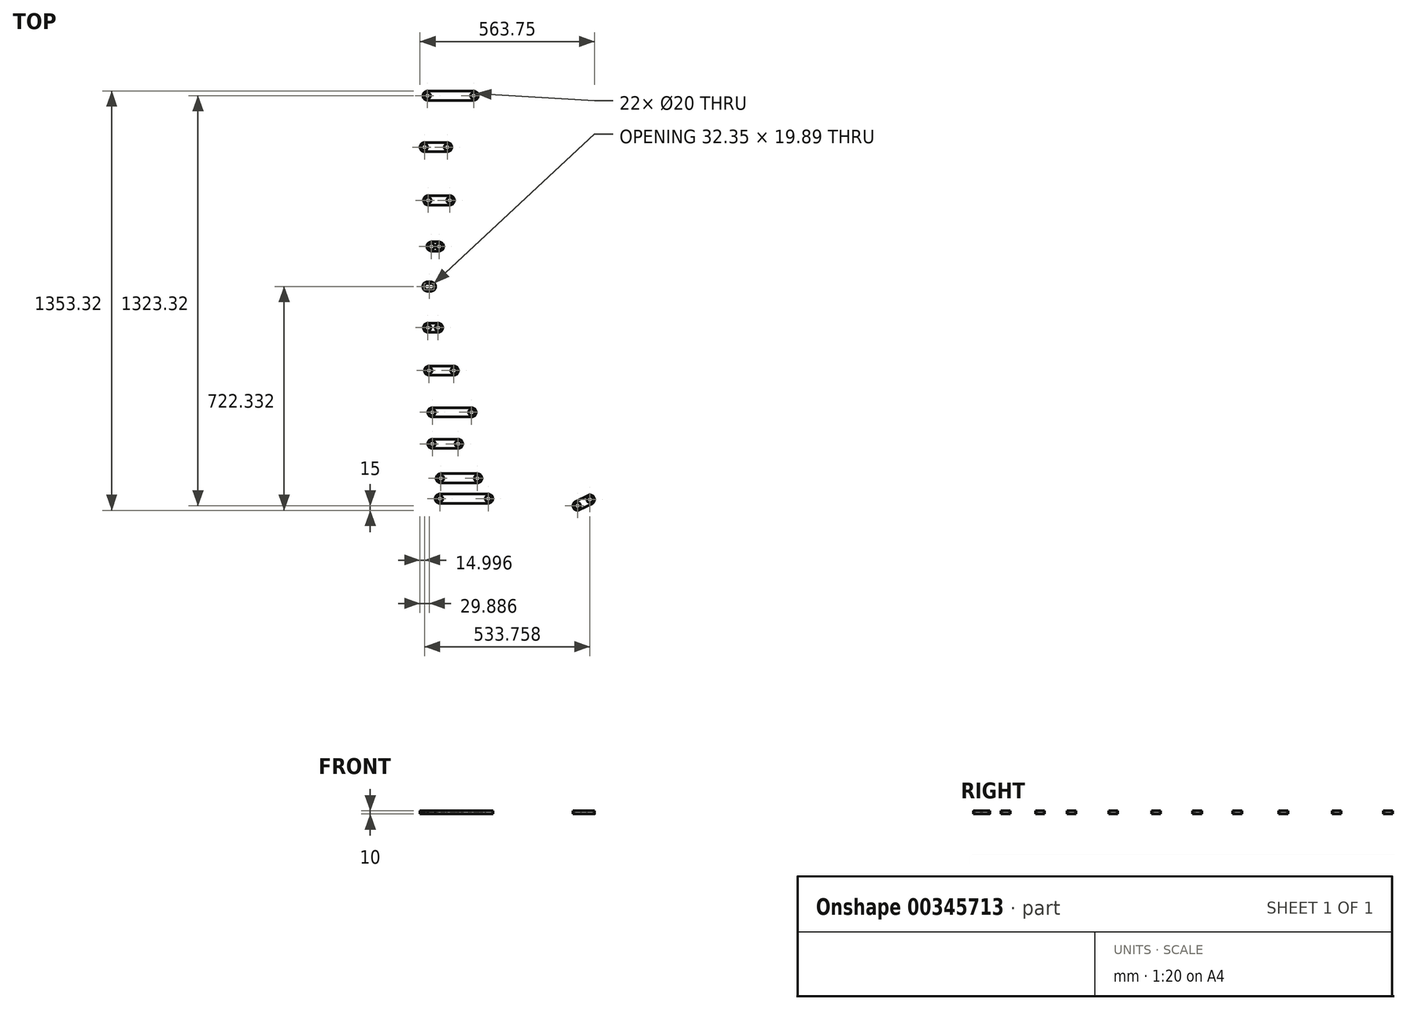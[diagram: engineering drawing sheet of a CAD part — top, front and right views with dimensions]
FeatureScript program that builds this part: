
annotation { "Feature Type Name" : "Feature", "Feature Type Description" : "" }
export const myFeature = defineFeature(function(context is Context, id is Id, definition is map)
    precondition{}
    {
        {
            var Q0;
            Q0=qCreatedBy(makeId("Top.planeOp"),FACE);
            var sketch = newSketch(context, id + "F0", { "sketchPlane" : qUnion([Q0])});
            skLineSegment(sketch, "E0", {"start": v(-109.53, 28.97) * mm, "end": v(46.83, 28.97) * mm});
            skCircle(sketch, "E1", {"center": v(-109.53, 28.97) * mm, "radius": 10 * mm});
            skCircle(sketch, "E2", {"center": v(46.83, 28.97) * mm, "radius": 10 * mm});
            skArc(sketch, "E3.0.startCap", {"start": v(-109.53, 13.97) * mm, "mid": v(-124.53, 28.97) * mm, "end": v(-109.53, 43.97) * mm});
            skArc(sketch, "E3.0.endCap", {"start": v(46.83, 43.97) * mm, "mid": v(61.83, 28.97) * mm, "end": v(46.83, 13.97) * mm});
            skLineSegment(sketch, "E3.0.left", {"start": v(-109.53, 43.97) * mm, "end": v(46.83, 43.97) * mm});
            skLineSegment(sketch, "E3.0.right", {"start": v(-109.53, 13.97) * mm, "end": v(46.83, 13.97) * mm});
            skLineSegment(sketch, "E4", {"start": v(-106.6, 94.85) * mm, "end": v(11.5, 94.85) * mm});
            skCircle(sketch, "E5", {"center": v(-106.6, 94.85) * mm, "radius": 10 * mm});
            skCircle(sketch, "E6", {"center": v(11.5, 94.85) * mm, "radius": 10 * mm});
            skArc(sketch, "E7.0.startCap", {"start": v(-106.6, 79.85) * mm, "mid": v(-121.6, 94.85) * mm, "end": v(-106.6, 109.85) * mm});
            skArc(sketch, "E7.0.endCap", {"start": v(11.5, 109.85) * mm, "mid": v(26.5, 94.85) * mm, "end": v(11.5, 79.85) * mm});
            skLineSegment(sketch, "E7.0.left", {"start": v(-106.6, 109.85) * mm, "end": v(11.5, 109.85) * mm});
            skLineSegment(sketch, "E7.0.right", {"start": v(-106.6, 79.85) * mm, "end": v(11.5, 79.85) * mm});
            skLineSegment(sketch, "E8", {"start": v(-133.71, 206.13) * mm, "end": v(-50.52, 206.13) * mm});
            skCircle(sketch, "E9", {"center": v(-133.71, 206.13) * mm, "radius": 10 * mm});
            skCircle(sketch, "E10", {"center": v(-50.52, 206.13) * mm, "radius": 10 * mm});
            skArc(sketch, "E11.0.startCap", {"start": v(-133.71, 191.13) * mm, "mid": v(-148.71, 206.13) * mm, "end": v(-133.71, 221.13) * mm});
            skArc(sketch, "E11.0.endCap", {"start": v(-50.52, 221.13) * mm, "mid": v(-35.52, 206.13) * mm, "end": v(-50.52, 191.13) * mm});
            skLineSegment(sketch, "E11.0.left", {"start": v(-133.71, 221.13) * mm, "end": v(-50.52, 221.13) * mm});
            skLineSegment(sketch, "E11.0.right", {"start": v(-133.71, 191.13) * mm, "end": v(-50.52, 191.13) * mm});
            skLineSegment(sketch, "E12", {"start": v(-133.71, 307.76) * mm, "end": v(-7.05, 307.76) * mm});
            skCircle(sketch, "E13", {"center": v(-133.71, 307.76) * mm, "radius": 10 * mm});
            skCircle(sketch, "E14", {"center": v(-7.05, 307.76) * mm, "radius": 10 * mm});
            skArc(sketch, "E15.0.startCap", {"start": v(-133.71, 292.76) * mm, "mid": v(-148.71, 307.76) * mm, "end": v(-133.71, 322.76) * mm});
            skArc(sketch, "E15.0.endCap", {"start": v(-7.05, 322.76) * mm, "mid": v(7.95, 307.76) * mm, "end": v(-7.05, 292.76) * mm});
            skLineSegment(sketch, "E15.0.left", {"start": v(-133.71, 322.76) * mm, "end": v(-7.05, 322.76) * mm});
            skLineSegment(sketch, "E15.0.right", {"start": v(-133.71, 292.76) * mm, "end": v(-7.05, 292.76) * mm});
            skLineSegment(sketch, "E16", {"start": v(-144.5, 442.43) * mm, "end": v(-64.5, 442.43) * mm});
            skCircle(sketch, "E17", {"center": v(-144.5, 442.43) * mm, "radius": 10 * mm});
            skCircle(sketch, "E18", {"center": v(-64.5, 442.43) * mm, "radius": 10 * mm});
            skArc(sketch, "E19.0.startCap", {"start": v(-144.5, 427.43) * mm, "mid": v(-159.5, 442.43) * mm, "end": v(-144.5, 457.43) * mm});
            skArc(sketch, "E19.0.endCap", {"start": v(-64.5, 457.43) * mm, "mid": v(-49.5, 442.43) * mm, "end": v(-64.5, 427.43) * mm});
            skLineSegment(sketch, "E19.0.left", {"start": v(-144.5, 457.43) * mm, "end": v(-64.5, 457.43) * mm});
            skLineSegment(sketch, "E19.0.right", {"start": v(-144.5, 427.43) * mm, "end": v(-64.5, 427.43) * mm});
            skLineSegment(sketch, "E20", {"start": v(-148, 580.85) * mm, "end": v(-115.18, 580.85) * mm});
            skCircle(sketch, "E21", {"center": v(-148, 580.85) * mm, "radius": 10 * mm});
            skCircle(sketch, "E22", {"center": v(-115.18, 580.85) * mm, "radius": 10 * mm});
            skArc(sketch, "E23.0.startCap", {"start": v(-148, 565.85) * mm, "mid": v(-163, 580.85) * mm, "end": v(-148, 595.85) * mm});
            skArc(sketch, "E23.0.endCap", {"start": v(-115.18, 595.85) * mm, "mid": v(-100.18, 580.85) * mm, "end": v(-115.18, 565.85) * mm});
            skLineSegment(sketch, "E23.0.left", {"start": v(-148, 595.85) * mm, "end": v(-115.18, 595.85) * mm});
            skLineSegment(sketch, "E23.0.right", {"start": v(-148, 565.85) * mm, "end": v(-115.18, 565.85) * mm});
            skLineSegment(sketch, "E24", {"start": v(-150.03, 713.57) * mm, "end": v(-137.68, 713.57) * mm});
            skCircle(sketch, "E25", {"center": v(-150.03, 713.57) * mm, "radius": 10 * mm});
            skCircle(sketch, "E26", {"center": v(-137.68, 713.57) * mm, "radius": 10 * mm});
            skArc(sketch, "E27.0.startCap", {"start": v(-150.03, 698.57) * mm, "mid": v(-165.03, 713.57) * mm, "end": v(-150.03, 728.57) * mm});
            skArc(sketch, "E27.0.endCap", {"start": v(-137.68, 728.57) * mm, "mid": v(-122.68, 713.57) * mm, "end": v(-137.68, 698.57) * mm});
            skLineSegment(sketch, "E27.0.left", {"start": v(-150.03, 728.57) * mm, "end": v(-137.68, 728.57) * mm});
            skLineSegment(sketch, "E27.0.right", {"start": v(-150.03, 698.57) * mm, "end": v(-137.68, 698.57) * mm});
            skLineSegment(sketch, "E28", {"start": v(-136.65, 842.88) * mm, "end": v(-111.94, 842.88) * mm});
            skCircle(sketch, "E29", {"center": v(-136.65, 842.88) * mm, "radius": 10 * mm});
            skCircle(sketch, "E30", {"center": v(-111.94, 842.88) * mm, "radius": 10 * mm});
            skArc(sketch, "E31.0.startCap", {"start": v(-136.65, 827.88) * mm, "mid": v(-151.65, 842.88) * mm, "end": v(-136.65, 857.88) * mm});
            skArc(sketch, "E31.0.endCap", {"start": v(-111.94, 857.88) * mm, "mid": v(-96.94, 842.88) * mm, "end": v(-111.94, 827.88) * mm});
            skLineSegment(sketch, "E31.0.left", {"start": v(-136.65, 857.88) * mm, "end": v(-111.94, 857.88) * mm});
            skLineSegment(sketch, "E31.0.right", {"start": v(-136.65, 827.88) * mm, "end": v(-111.94, 827.88) * mm});
            skLineSegment(sketch, "E32", {"start": v(-147.52, 991.9) * mm, "end": v(-77.29, 991.9) * mm});
            skCircle(sketch, "E33", {"center": v(-147.52, 991.9) * mm, "radius": 10 * mm});
            skCircle(sketch, "E34", {"center": v(-77.29, 991.9) * mm, "radius": 10 * mm});
            skArc(sketch, "E35.0.startCap", {"start": v(-147.52, 976.9) * mm, "mid": v(-162.52, 991.9) * mm, "end": v(-147.52, 1006.9) * mm});
            skArc(sketch, "E35.0.endCap", {"start": v(-77.29, 1006.9) * mm, "mid": v(-62.29, 991.9) * mm, "end": v(-77.29, 976.9) * mm});
            skLineSegment(sketch, "E35.0.left", {"start": v(-147.52, 1006.9) * mm, "end": v(-77.29, 1006.9) * mm});
            skLineSegment(sketch, "E35.0.right", {"start": v(-147.52, 976.9) * mm, "end": v(-77.29, 976.9) * mm});
            skLineSegment(sketch, "E36", {"start": v(-158.74, 1163.7) * mm, "end": v(-85.49, 1163.7) * mm});
            skCircle(sketch, "E37", {"center": v(-158.74, 1163.7) * mm, "radius": 10 * mm});
            skCircle(sketch, "E38", {"center": v(-85.49, 1163.7) * mm, "radius": 10 * mm});
            skArc(sketch, "E39.0.startCap", {"start": v(-158.74, 1148.7) * mm, "mid": v(-173.74, 1163.7) * mm, "end": v(-158.74, 1178.7) * mm});
            skArc(sketch, "E39.0.endCap", {"start": v(-85.49, 1178.7) * mm, "mid": v(-70.49, 1163.7) * mm, "end": v(-85.49, 1148.7) * mm});
            skLineSegment(sketch, "E39.0.left", {"start": v(-158.74, 1178.7) * mm, "end": v(-85.49, 1178.7) * mm});
            skLineSegment(sketch, "E39.0.right", {"start": v(-158.74, 1148.7) * mm, "end": v(-85.49, 1148.7) * mm});
            skLineSegment(sketch, "E40", {"start": v(-149.42, 1329.56) * mm, "end": v(-0.32, 1329.56) * mm});
            skCircle(sketch, "E41", {"center": v(-149.42, 1329.56) * mm, "radius": 10 * mm});
            skCircle(sketch, "E42", {"center": v(-0.32, 1329.56) * mm, "radius": 10 * mm});
            skArc(sketch, "E43.0.startCap", {"start": v(-149.42, 1314.56) * mm, "mid": v(-164.42, 1329.56) * mm, "end": v(-149.42, 1344.56) * mm});
            skArc(sketch, "E43.0.endCap", {"start": v(-0.32, 1344.56) * mm, "mid": v(14.68, 1329.56) * mm, "end": v(-0.32, 1314.56) * mm});
            skLineSegment(sketch, "E43.0.left", {"start": v(-149.42, 1344.56) * mm, "end": v(-0.32, 1344.56) * mm});
            skLineSegment(sketch, "E43.0.right", {"start": v(-149.42, 1314.56) * mm, "end": v(-0.32, 1314.56) * mm});
            skLineSegment(sketch, "E44", {"start": v(335.01, 6.24) * mm, "end": v(375.01, 26.24) * mm});
            skCircle(sketch, "E45", {"center": v(335.01, 6.24) * mm, "radius": 10 * mm});
            skCircle(sketch, "E46", {"center": v(375.01, 26.24) * mm, "radius": 10 * mm});
            skArc(sketch, "E47.0.startCap", {"start": v(341.72, -7.18) * mm, "mid": v(321.6, -0.47) * mm, "end": v(328.3, 19.66) * mm});
            skArc(sketch, "E47.0.endCap", {"start": v(368.3, 39.66) * mm, "mid": v(388.43, 32.95) * mm, "end": v(381.72, 12.82) * mm});
            skLineSegment(sketch, "E47.0.left", {"start": v(328.3, 19.66) * mm, "end": v(368.3, 39.66) * mm});
            skLineSegment(sketch, "E47.0.right", {"start": v(341.72, -7.18) * mm, "end": v(381.72, 12.82) * mm});
            skLineSegment(sketch, "E48", {"start": v(335.01, 6.24) * mm, "end": v(335.01, 26.24) * mm, "construction": true});
            skPoint(sketch, "E48.endSnap0", {"position": v(335.01, -6.93) * mm});
            skLineSegment(sketch, "E49", {"start": v(335.01, 26.24) * mm, "end": v(375.01, 26.24) * mm, "construction": true});
            skLineSegment(sketch, "E50", {"start": v(425.26, 26.24) * mm, "end": v(481.54, 26.24) * mm});
            skSolve(sketch);
        }
        {
            var Q0;
            Q0 = qSketchRegion(id + "F0", true);
            extrude(context, id + "F1", {"entities" : qUnion([Q0]), "depth" : 10 * mm});
        }
    });
